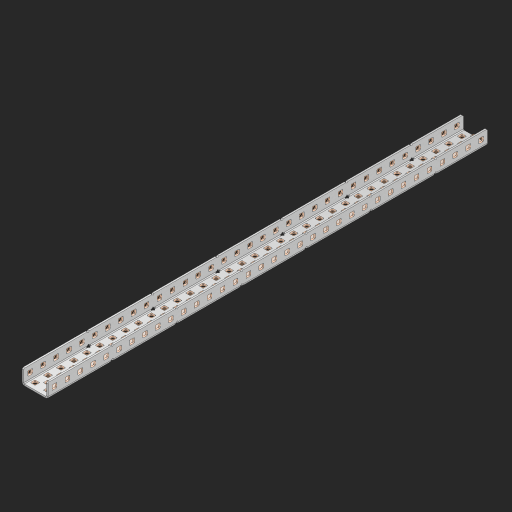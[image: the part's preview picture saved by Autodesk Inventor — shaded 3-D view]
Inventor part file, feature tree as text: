
AUTODESK INVENTOR PART (.ipt)
format: ipt  version: 2023 (Build 270158000, 158)  size: 2,074,112 bytes
history: native  units: in
note: dims shown in document units (in); Inventor stores cm internally (conversion verified against a paired STEP export)
features: other x177, extrude x168, sheet_metal_op x11, sketch x10, pattern_linear x2, mirror x1, chamfer x1
ambient origin geometry x8: Origin, YZ Plane, XZ Plane, XY Plane, X Axis, Y Axis, Z Axis, Center Point
bodies: Solid1 (feature_tree), Body (feature_tree)
feature tree (370):
  sheet_metal_op  "Flanges"
  other  "Flange Pattern Plane"
  other  "Flange Pattern Sketch"
  sheet_metal_op  "Flange Pattern"
  sheet_metal_op  "Body Pattern"
  pattern_linear  "Center Pattern"  Spacing1=0.0625in  [1 undecoded]
  other  "Arc Length"
  mirror  "Notch Mirror"
  pattern_linear  "Notch Pattern"  Spacing1=0.182in  [1 undecoded]
  chamfer  "End Chamfer"
  extrude  "Half Cut"  Depth=0.02in
  sketch  "Sketch1"  dims[d0=1.0in]
  other  "Plate1"
  sketch  "Sketch2"  dims[d1=17.0in]
  other  "Plate2"
  sheet_metal_op  "Bend1"
  sheet_metal_op  "Corner1"
  sketch  "Sketch3"  dims[d2=0.0625in]
  sketch  "Sketch7"  dims[d3=0.0625in]
  other  "Srf1"
  other  "Srf2"
  sketch  "Sketch8"  dims[d4=0.0312in]
  sketch  "Sketch9"  dims[d5=0.125in]
  other  "Srf91"
  sheet_metal_op  "Body Pattern Sketch"
  other  "Srf92"
  sketch  "Sketch13"  dims[d6=0.0625in]
  sketch  "Sketch14"  dims[d7=0.5in d8=90.0deg d9=0.0312in]
  sketch  "Sketch15"  dims[d10=0.25in]
  sketch  "Sketch16"  dims[d11=0.0625in d12=0.0625in d16=0.182in d17=0.02in d18=0.0625in d19=0.0in d20=0.25in d21=0.25in d38=13.3858in d40=0.5in d41=0.7874in d43=1.0in d46=0.172in d47=1.0in d48=0.0in d49=0.182in d50=0.02in d51=0.25in d52=0.25in d53=0.0625in d54=0.0in d55=0.172in d56=1.0in d57=0.0in d58=0.25in d60=13.3858in d62=0.5in d63=0.7874in d65=0.5in d85=0.1473in d86=0.1782in d88=0.04in d89=0.0625in d90=0.0in d91=0.04in d92=0.0491in d95=2.5in d96=0.04in d97=0.25in d98=45.0deg d99=0.25in d100=0.5in d101=0.0in d102=2.497in d106=0.182in d107=0.02in d108=0.5in d109=0.5in d110=0.0625in d111=0.0in d112=0.172in d113=0.5in d114=0.0in d117=0.5in d118=0.5in d119=0.5in]
  other  "Srf786"
  other  "Srf823"
  other  "Srf824"
  other  "Srf825"
  other  "Srf826"
  other  "Srf827"
  other  "Srf828"
  other  "Srf829"
  other  "Srf856"
  other  "Srf857"
  other  "Srf858"
  other  "Srf859"
  other  "Srf860"
  other  "Srf861"
  other  "Srf862"
  other  "Srf889"
  other  "Srf890"
  other  "Srf891"
  other  "Srf892"
  other  "Srf893"
  other  "Srf894"
  other  "Srf895"
  other  "Srf896"
  other  "Srf922"
  other  "Srf923"
  other  "Srf924"
  other  "Srf925"
  other  "Srf926"
  other  "Srf959"
  other  "Srf960"
  other  "Srf961"
  other  "Srf962"
  other  "Srf963"
  other  "Srf996"
  other  "Srf997"
  other  "Srf998"
  other  "Srf999"
  other  "Srf1000"
  other  "Srf1143"
  other  "Srf1144"
  other  "Srf1145"
  other  "Srf1146"
  other  "Srf1147"
  other  "Srf1148"
  other  "Srf1149"
  other  "Srf1150"
  other  "Srf1151"
  other  "Srf1152"
  other  "Srf1153"
  other  "Srf1154"
  other  "Srf1155"
  other  "Srf1156"
  other  "Srf1157"
  other  "Srf1158"
  other  "Srf1159"
  other  "Srf1160"
  other  "Srf1161"
  other  "Srf1162"
  other  "Srf1163"
  other  "Srf1164"
  other  "Srf1165"
  other  "Srf1166"
  other  "Srf1167"
  other  "Srf1168"
  other  "Srf1169"
  other  "Srf1170"
  other  "Srf1171"
  other  "Srf1172"
  other  "Srf1173"
  other  "Srf1174"
  other  "Srf1175"
  other  "Srf1176"
  other  "Srf1177"
  other  "Srf1178"
  other  "Srf1179"
  other  "Srf1180"
  other  "Srf1181"
  other  "Srf1182"
  other  "Srf1183"
  other  "Srf1184"
  other  "Srf1185"
  other  "Srf1186"
  other  "Srf1187"
  other  "Srf1188"
  other  "Srf1189"
  other  "Srf1190"
  other  "Srf1191"
  other  "Srf1192"
  other  "Srf1193"
  other  "Srf1194"
  other  "Srf1195"
  other  "Srf1196"
  other  "Srf1199"
  other  "Srf1200"
  other  "Srf1201"
  other  "Srf1202"
  other  "Srf1203"
  other  "Srf1204"
  other  "Srf1205"
  other  "Srf1206"
  other  "Srf1207"
  other  "Srf1208"
  other  "Srf1209"
  other  "Srf1210"
  other  "Srf1211"
  other  "Srf1212"
  other  "Srf1213"
  other  "Srf1214"
  other  "Srf1215"
  other  "Srf1216"
  other  "Srf1217"
  other  "Srf1218"
  other  "Srf1219"
  other  "Srf1220"
  other  "Srf1221"
  other  "Srf1222"
  other  "Srf1223"
  other  "Srf1224"
  other  "Srf1225"
  other  "Srf1226"
  other  "Srf1227"
  other  "Srf1228"
  other  "Srf1229"
  other  "Srf1230"
  other  "Srf1231"
  other  "Srf1232"
  other  "Srf1233"
  other  "Srf1234"
  other  "Srf1235"
  other  "Srf1236"
  other  "Srf1237"
  other  "Srf1238"
  other  "Srf1239"
  other  "Srf1240"
  other  "Srf1241"
  other  "Srf1242"
  other  "Srf1243"
  other  "Srf1244"
  other  "Srf1245"
  other  "Srf1246"
  other  "Srf1247"
  other  "Srf1248"
  other  "Srf1249"
  other  "Srf1250"
  other  "Srf1251"
  other  "Srf1252"
  other  "Srf1255"
  other  "Srf1256"
  other  "Srf1257"
  other  "Srf1258"
  other  "Srf1259"
  other  "Srf1260"
  other  "Srf1261"
  other  "Srf1262"
  other  "Srf1263"
  other  "Srf1264"
  other  "Srf1265"
  other  "Srf1266"
  other  "Srf1267"
  other  "Srf1268"
  other  "Srf1269"
  other  "Srf1270"
  other  "Srf1271"
  other  "Srf1272"
  other  "Srf1273"
  other  "Srf1274"
  sheet_metal_op  "Flange Stamp"
  sheet_metal_op  "Flange Circle"
  sheet_metal_op  "Body Stamp"
  sheet_metal_op  "Body Circle"
  other  "Center Stamp"
  other  "Center Circle"
  sheet_metal_op  "Notch"
  extrude  "ExtrusionSrf2"  Depth=0.0625in
  extrude  "ExtrusionSrf92"  TaperAngle=0.0deg  [1 undecoded]
  extrude  "ExtrusionSrf823"  Depth=0.5in
  extrude  "ExtrusionSrf824"  Depth=0.5in
  extrude  "ExtrusionSrf825"  Depth=0.5in
  extrude  "ExtrusionSrf826"  Depth=0.5in
  extrude  "ExtrusionSrf827"  Depth=1.0in TaperAngle=0.0deg
  extrude  "ExtrusionSrf828"  Depth=0.5in
  extrude  "ExtrusionSrf829"  Depth=0.02in
  extrude  "ExtrusionSrf856"  Depth=0.5in
  extrude  "ExtrusionSrf857"  Depth=0.5in
  extrude  "ExtrusionSrf858"  Depth=0.0625in
  extrude  "ExtrusionSrf859"  TaperAngle=0.0deg  [1 undecoded]
  extrude  "ExtrusionSrf860"  Depth=0.5in
  extrude  "ExtrusionSrf861"  Depth=1.0in TaperAngle=0.0deg
  extrude  "ExtrusionSrf862"  Depth=0.5in
  extrude  "ExtrusionSrf889"  Depth=0.5in
  extrude  "ExtrusionSrf890"  Depth=0.5in
  extrude  "ExtrusionSrf891"  Depth=0.5in
  extrude  "ExtrusionSrf892"  Depth=0.5in
  extrude  "ExtrusionSrf893"  Depth=0.5in
  extrude  "ExtrusionSrf894"  Depth=0.0625in
  extrude  "ExtrusionSrf895"  TaperAngle=0.0deg  [1 undecoded]
  extrude  "ExtrusionSrf896"  Depth=0.5in
  extrude  "ExtrusionSrf922"  Depth=0.5in
  extrude  "ExtrusionSrf923"  Depth=2.5in
  extrude  "ExtrusionSrf924"  Depth=0.5in TaperAngle=45.0deg
  extrude  "ExtrusionSrf925"  Depth=0.5in
  extrude  "ExtrusionSrf926"  Depth=0.5in TaperAngle=0.0deg
  extrude  "ExtrusionSrf959"  Depth=0.5in
  extrude  "ExtrusionSrf960"  Depth=0.5in
  extrude  "ExtrusionSrf961"  Depth=0.02in
  extrude  "ExtrusionSrf962"  Depth=0.5in
  extrude  "ExtrusionSrf963"  Depth=0.5in
  extrude  "ExtrusionSrf996"  Depth=0.0625in
  extrude  "ExtrusionSrf997"  TaperAngle=0.0deg  [1 undecoded]
  extrude  "ExtrusionSrf998"  Depth=0.5in
  extrude  "ExtrusionSrf999"  Depth=0.5in TaperAngle=0.0deg
  extrude  "ExtrusionSrf1000"  Depth=0.5in
  extrude  "ExtrusionSrf1143"  Depth=0.5in
  extrude  "ExtrusionSrf1144"  Depth=0.5in
  extrude  "ExtrusionSrf1145"  [1 undecoded]
  extrude  "ExtrusionSrf1146"  [1 undecoded]
  extrude  "ExtrusionSrf1147"  [1 undecoded]
  extrude  "ExtrusionSrf1148"  [1 undecoded]
  extrude  "ExtrusionSrf1149"  [1 undecoded]
  extrude  "ExtrusionSrf1150"  [1 undecoded]
  extrude  "ExtrusionSrf1151"  [1 undecoded]
  extrude  "ExtrusionSrf1152"  [1 undecoded]
  extrude  "ExtrusionSrf1153"  [1 undecoded]
  extrude  "ExtrusionSrf1154"  [1 undecoded]
  extrude  "ExtrusionSrf1155"  [1 undecoded]
  extrude  "ExtrusionSrf1156"  [1 undecoded]
  extrude  "ExtrusionSrf1157"  [1 undecoded]
  extrude  "ExtrusionSrf1158"  [1 undecoded]
  extrude  "ExtrusionSrf1159"  [1 undecoded]
  extrude  "ExtrusionSrf1160"  [1 undecoded]
  extrude  "ExtrusionSrf1161"  [1 undecoded]
  extrude  "ExtrusionSrf1162"  [1 undecoded]
  extrude  "ExtrusionSrf1163"  [1 undecoded]
  extrude  "ExtrusionSrf1164"  [1 undecoded]
  extrude  "ExtrusionSrf1165"  [1 undecoded]
  extrude  "ExtrusionSrf1166"  [1 undecoded]
  extrude  "ExtrusionSrf1167"  [1 undecoded]
  extrude  "ExtrusionSrf1168"  [1 undecoded]
  extrude  "ExtrusionSrf1169"  [1 undecoded]
  extrude  "ExtrusionSrf1170"  [1 undecoded]
  extrude  "ExtrusionSrf1171"  [1 undecoded]
  extrude  "ExtrusionSrf1172"  [1 undecoded]
  extrude  "ExtrusionSrf1173"  [1 undecoded]
  extrude  "ExtrusionSrf1174"  [1 undecoded]
  extrude  "ExtrusionSrf1175"  [1 undecoded]
  extrude  "ExtrusionSrf1176"  [1 undecoded]
  extrude  "ExtrusionSrf1177"  [1 undecoded]
  extrude  "ExtrusionSrf1178"  [1 undecoded]
  extrude  "ExtrusionSrf1179"  [1 undecoded]
  extrude  "ExtrusionSrf1180"  [1 undecoded]
  extrude  "ExtrusionSrf1181"  [1 undecoded]
  extrude  "ExtrusionSrf1182"  [1 undecoded]
  extrude  "ExtrusionSrf1183"  [1 undecoded]
  extrude  "ExtrusionSrf1184"  [1 undecoded]
  extrude  "ExtrusionSrf1185"  [1 undecoded]
  extrude  "ExtrusionSrf1186"  [1 undecoded]
  extrude  "ExtrusionSrf1187"  [1 undecoded]
  extrude  "ExtrusionSrf1188"  [1 undecoded]
  extrude  "ExtrusionSrf1189"  [1 undecoded]
  extrude  "ExtrusionSrf1190"  [1 undecoded]
  extrude  "ExtrusionSrf1191"  [1 undecoded]
  extrude  "ExtrusionSrf1192"  [1 undecoded]
  extrude  "ExtrusionSrf1193"  [1 undecoded]
  extrude  "ExtrusionSrf1194"  [1 undecoded]
  extrude  "ExtrusionSrf1195"  [1 undecoded]
  extrude  "ExtrusionSrf1196"  [1 undecoded]
  extrude  "ExtrusionSrf1199"  [1 undecoded]
  extrude  "ExtrusionSrf1200"  [1 undecoded]
  extrude  "ExtrusionSrf1201"  [1 undecoded]
  extrude  "ExtrusionSrf1202"  [1 undecoded]
  extrude  "ExtrusionSrf1203"  [1 undecoded]
  extrude  "ExtrusionSrf1204"  [1 undecoded]
  extrude  "ExtrusionSrf1205"  [1 undecoded]
  extrude  "ExtrusionSrf1206"  [1 undecoded]
  extrude  "ExtrusionSrf1207"  [1 undecoded]
  extrude  "ExtrusionSrf1208"  [1 undecoded]
  extrude  "ExtrusionSrf1209"  [1 undecoded]
  extrude  "ExtrusionSrf1210"  [1 undecoded]
  extrude  "ExtrusionSrf1211"  [1 undecoded]
  extrude  "ExtrusionSrf1212"  [1 undecoded]
  extrude  "ExtrusionSrf1213"  [1 undecoded]
  extrude  "ExtrusionSrf1214"  [1 undecoded]
  extrude  "ExtrusionSrf1215"  [1 undecoded]
  extrude  "ExtrusionSrf1216"  [1 undecoded]
  extrude  "ExtrusionSrf1217"  [1 undecoded]
  extrude  "ExtrusionSrf1218"  [1 undecoded]
  extrude  "ExtrusionSrf1219"  [1 undecoded]
  extrude  "ExtrusionSrf1220"  [1 undecoded]
  extrude  "ExtrusionSrf1221"  [1 undecoded]
  extrude  "ExtrusionSrf1222"  [1 undecoded]
  extrude  "ExtrusionSrf1223"  [1 undecoded]
  extrude  "ExtrusionSrf1224"  [1 undecoded]
  extrude  "ExtrusionSrf1225"  [1 undecoded]
  extrude  "ExtrusionSrf1226"  [1 undecoded]
  extrude  "ExtrusionSrf1227"  [1 undecoded]
  extrude  "ExtrusionSrf1228"  [1 undecoded]
  extrude  "ExtrusionSrf1229"  [1 undecoded]
  extrude  "ExtrusionSrf1230"  [1 undecoded]
  extrude  "ExtrusionSrf1231"  [1 undecoded]
  extrude  "ExtrusionSrf1232"  [1 undecoded]
  extrude  "ExtrusionSrf1233"  [1 undecoded]
  extrude  "ExtrusionSrf1234"  [1 undecoded]
  extrude  "ExtrusionSrf1235"  [1 undecoded]
  extrude  "ExtrusionSrf1236"  [1 undecoded]
  extrude  "ExtrusionSrf1237"  [1 undecoded]
  extrude  "ExtrusionSrf1238"  [1 undecoded]
  extrude  "ExtrusionSrf1239"  [1 undecoded]
  extrude  "ExtrusionSrf1240"  [1 undecoded]
  extrude  "ExtrusionSrf1241"  [1 undecoded]
  extrude  "ExtrusionSrf1242"  [1 undecoded]
  extrude  "ExtrusionSrf1243"  [1 undecoded]
  extrude  "ExtrusionSrf1244"  [1 undecoded]
  extrude  "ExtrusionSrf1245"  [1 undecoded]
  extrude  "ExtrusionSrf1246"  [1 undecoded]
  extrude  "ExtrusionSrf1247"  [1 undecoded]
  extrude  "ExtrusionSrf1248"  [1 undecoded]
  extrude  "ExtrusionSrf1249"  [1 undecoded]
  extrude  "ExtrusionSrf1250"  [1 undecoded]
  extrude  "ExtrusionSrf1251"  [1 undecoded]
  extrude  "ExtrusionSrf1252"  [1 undecoded]
  extrude  "ExtrusionSrf1255"  [1 undecoded]
  extrude  "ExtrusionSrf1256"  [1 undecoded]
  extrude  "ExtrusionSrf1257"  [1 undecoded]
  extrude  "ExtrusionSrf1258"  [1 undecoded]
  extrude  "ExtrusionSrf1259"  [1 undecoded]
  extrude  "ExtrusionSrf1260"  [1 undecoded]
  extrude  "ExtrusionSrf1261"  [1 undecoded]
  extrude  "ExtrusionSrf1262"  [1 undecoded]
  extrude  "ExtrusionSrf1263"  [1 undecoded]
  extrude  "ExtrusionSrf1264"  [1 undecoded]
  extrude  "ExtrusionSrf1265"  [1 undecoded]
  extrude  "ExtrusionSrf1266"  [1 undecoded]
  extrude  "ExtrusionSrf1267"  [1 undecoded]
  extrude  "ExtrusionSrf1268"  [1 undecoded]
  extrude  "ExtrusionSrf1269"  [1 undecoded]
  extrude  "ExtrusionSrf1270"  [1 undecoded]
  extrude  "ExtrusionSrf1271"  [1 undecoded]
  extrude  "ExtrusionSrf1272"  [1 undecoded]
  extrude  "ExtrusionSrf1273"  [1 undecoded]
  extrude  "ExtrusionSrf1274"  [1 undecoded]
note: 132 required parameter values undecoded (feature->parameter linkage not recoverable at this tier; creation-order binding heuristic only, values carry confidence <= 0.55)
